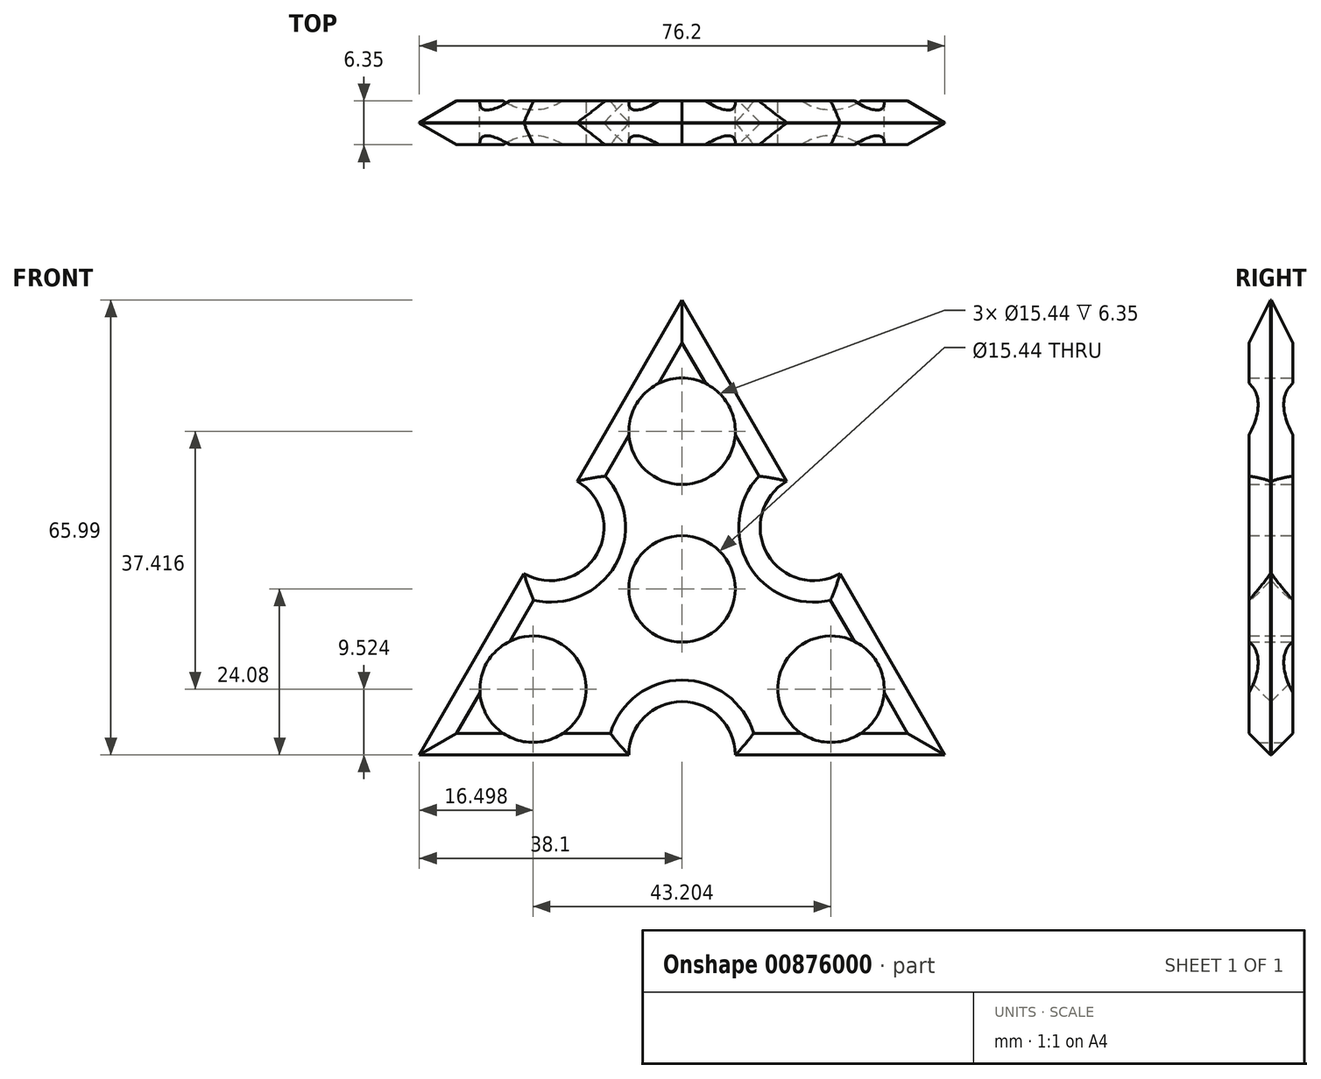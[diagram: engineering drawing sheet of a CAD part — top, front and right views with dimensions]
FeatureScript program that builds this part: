
annotation { "Feature Type Name" : "Feature", "Feature Type Description" : "" }
export const myFeature = defineFeature(function(context is Context, id is Id, definition is map)
    precondition{}
    {
        {
            var Q0;
            Q0=qCreatedBy(makeId("Front.planeOp"),FACE);
            var sketch = newSketch(context, id + "F0", { "sketchPlane" : qUnion([Q0])});
            skLineSegment(sketch, "E0", {"start": v(-38.1, -24.08) * mm, "end": v(0, 41.91) * mm});
            skLineSegment(sketch, "E1", {"start": v(0, 41.91) * mm, "end": v(38.1, -24.08) * mm});
            skLineSegment(sketch, "E2", {"start": v(38.1, -24.08) * mm, "end": v(-38.1, -24.08) * mm});
            skCircle(sketch, "E3", {"center": v(0, 22.86) * mm, "radius": 7.72 * mm});
            skCircle(sketch, "E4", {"center": v(21.6, -14.56) * mm, "radius": 7.72 * mm});
            skCircle(sketch, "E5", {"center": v(-21.6, -14.56) * mm, "radius": 7.72 * mm});
            skCircle(sketch, "E6", {"center": v(0, 0) * mm, "radius": 7.72 * mm});
            skCircle(sketch, "E7", {"center": v(-19.05, 8.91) * mm, "radius": 7.72 * mm});
            skCircle(sketch, "E8", {"center": v(19.05, 8.91) * mm, "radius": 7.72 * mm});
            skCircle(sketch, "E9", {"center": v(0, -24.08) * mm, "radius": 7.72 * mm});
            skSolve(sketch);
        }
        {
            var Q0;
            Q0=makeQuery(id+"F0.imprint","IMPRINT",FACE,{"disambiguationData":[TD([[makeQuery(id+"F0.imprint","IMPRINT",EDGE,{"derivedFrom":sQuery(id+"F0.wireOp",EDGE,"E3")}),-1.0]])]});
            extrude(context, id + "F1", {"entities" : qUnion([Q0]), "depth" : 6.35 * mm, "offsetDistance" : 25.4 * mm});
        }
        {
            var Q0;
            {var subQ0=sQuery(id+"F0.wireOp",EDGE,"E0");Q0=makeQuery(id+"F1.opExtrude","CAP_EDGE",EDGE,{"disambiguationData":[OSD([subQ0]),TDD([makeQuery(id+"F0.imprint","IMPRINT",EDGE,{"disambiguationData":[TD([[makeQuery(id+"F0.imprint","INTERSECT",VERTEX,{"derivedFrom":[subQ0,sQuery(id+"F0.wireOp",EDGE,"E2")]}),-1.0]])],"derivedFrom":subQ0})])],"isStart":false});}
            var Q1;
            Q1=makeQuery(id+"F1.opExtrude","CAP_EDGE",EDGE,{"disambiguationData":[OSD([sQuery(id+"F0.wireOp",EDGE,"E7")])],"isStart":false});
            var Q2;
            {var subQ0=sQuery(id+"F0.wireOp",EDGE,"E0");Q2=makeQuery(id+"F1.opExtrude","CAP_EDGE",EDGE,{"disambiguationData":[OSD([subQ0]),TDD([makeQuery(id+"F0.imprint","IMPRINT",EDGE,{"disambiguationData":[TD([[makeQuery(id+"F0.imprint","INTERSECT",VERTEX,{"derivedFrom":[subQ0,sQuery(id+"F0.wireOp",EDGE,"E1")]}),1.0]])],"derivedFrom":subQ0})])],"isStart":false});}
            var Q3;
            {var subQ0=sQuery(id+"F0.wireOp",EDGE,"E1");Q3=makeQuery(id+"F1.opExtrude","CAP_EDGE",EDGE,{"disambiguationData":[OSD([subQ0]),TDD([makeQuery(id+"F0.imprint","IMPRINT",EDGE,{"disambiguationData":[TD([[makeQuery(id+"F0.imprint","INTERSECT",VERTEX,{"derivedFrom":[sQuery(id+"F0.wireOp",EDGE,"E0"),subQ0]}),-1.0]])],"derivedFrom":subQ0})])],"isStart":false});}
            var Q4;
            Q4=makeQuery(id+"F1.opExtrude","CAP_EDGE",EDGE,{"disambiguationData":[OSD([sQuery(id+"F0.wireOp",EDGE,"E8")])],"isStart":false});
            var Q5;
            {var subQ0=sQuery(id+"F0.wireOp",EDGE,"E1");Q5=makeQuery(id+"F1.opExtrude","CAP_EDGE",EDGE,{"disambiguationData":[OSD([subQ0]),TDD([makeQuery(id+"F0.imprint","IMPRINT",EDGE,{"disambiguationData":[TD([[makeQuery(id+"F0.imprint","INTERSECT",VERTEX,{"derivedFrom":[subQ0,sQuery(id+"F0.wireOp",EDGE,"E2")]}),1.0]])],"derivedFrom":subQ0})])],"isStart":false});}
            var Q6;
            {var subQ0=sQuery(id+"F0.wireOp",EDGE,"E2");Q6=makeQuery(id+"F1.opExtrude","CAP_EDGE",EDGE,{"disambiguationData":[OSD([subQ0]),TDD([makeQuery(id+"F0.imprint","IMPRINT",EDGE,{"disambiguationData":[TD([[makeQuery(id+"F0.imprint","INTERSECT",VERTEX,{"derivedFrom":[sQuery(id+"F0.wireOp",EDGE,"E1"),subQ0]}),-1.0]])],"derivedFrom":subQ0})])],"isStart":false});}
            var Q7;
            Q7=makeQuery(id+"F1.opExtrude","CAP_EDGE",EDGE,{"disambiguationData":[OSD([sQuery(id+"F0.wireOp",EDGE,"E9")])],"isStart":false});
            var Q8;
            {var subQ0=sQuery(id+"F0.wireOp",EDGE,"E2");Q8=makeQuery(id+"F1.opExtrude","CAP_EDGE",EDGE,{"disambiguationData":[OSD([subQ0]),TDD([makeQuery(id+"F0.imprint","IMPRINT",EDGE,{"disambiguationData":[TD([[makeQuery(id+"F0.imprint","INTERSECT",VERTEX,{"derivedFrom":[sQuery(id+"F0.wireOp",EDGE,"E0"),subQ0]}),1.0]])],"derivedFrom":subQ0})])],"isStart":false});}
            var Q9;
            {var subQ0=sQuery(id+"F0.wireOp",EDGE,"E2");Q9=makeQuery(id+"F1.opExtrude","CAP_EDGE",EDGE,{"disambiguationData":[OSD([subQ0]),TDD([makeQuery(id+"F0.imprint","IMPRINT",EDGE,{"disambiguationData":[TD([[makeQuery(id+"F0.imprint","INTERSECT",VERTEX,{"derivedFrom":[sQuery(id+"F0.wireOp",EDGE,"E0"),subQ0]}),1.0]])],"derivedFrom":subQ0})])],"isStart":true});}
            var Q10;
            Q10=makeQuery(id+"F1.opExtrude","CAP_EDGE",EDGE,{"disambiguationData":[OSD([sQuery(id+"F0.wireOp",EDGE,"E9")])],"isStart":true});
            var Q11;
            {var subQ0=sQuery(id+"F0.wireOp",EDGE,"E2");Q11=makeQuery(id+"F1.opExtrude","CAP_EDGE",EDGE,{"disambiguationData":[OSD([subQ0]),TDD([makeQuery(id+"F0.imprint","IMPRINT",EDGE,{"disambiguationData":[TD([[makeQuery(id+"F0.imprint","INTERSECT",VERTEX,{"derivedFrom":[sQuery(id+"F0.wireOp",EDGE,"E1"),subQ0]}),-1.0]])],"derivedFrom":subQ0})])],"isStart":true});}
            var Q12;
            {var subQ0=sQuery(id+"F0.wireOp",EDGE,"E1");Q12=makeQuery(id+"F1.opExtrude","CAP_EDGE",EDGE,{"disambiguationData":[OSD([subQ0]),TDD([makeQuery(id+"F0.imprint","IMPRINT",EDGE,{"disambiguationData":[TD([[makeQuery(id+"F0.imprint","INTERSECT",VERTEX,{"derivedFrom":[subQ0,sQuery(id+"F0.wireOp",EDGE,"E2")]}),1.0]])],"derivedFrom":subQ0})])],"isStart":true});}
            var Q13;
            Q13=makeQuery(id+"F1.opExtrude","CAP_EDGE",EDGE,{"disambiguationData":[OSD([sQuery(id+"F0.wireOp",EDGE,"E8")])],"isStart":true});
            var Q14;
            {var subQ0=sQuery(id+"F0.wireOp",EDGE,"E1");Q14=makeQuery(id+"F1.opExtrude","CAP_EDGE",EDGE,{"disambiguationData":[OSD([subQ0]),TDD([makeQuery(id+"F0.imprint","IMPRINT",EDGE,{"disambiguationData":[TD([[makeQuery(id+"F0.imprint","INTERSECT",VERTEX,{"derivedFrom":[sQuery(id+"F0.wireOp",EDGE,"E0"),subQ0]}),-1.0]])],"derivedFrom":subQ0})])],"isStart":true});}
            var Q15;
            {var subQ0=sQuery(id+"F0.wireOp",EDGE,"E0");Q15=makeQuery(id+"F1.opExtrude","CAP_EDGE",EDGE,{"disambiguationData":[OSD([subQ0]),TDD([makeQuery(id+"F0.imprint","IMPRINT",EDGE,{"disambiguationData":[TD([[makeQuery(id+"F0.imprint","INTERSECT",VERTEX,{"derivedFrom":[subQ0,sQuery(id+"F0.wireOp",EDGE,"E1")]}),1.0]])],"derivedFrom":subQ0})])],"isStart":true});}
            var Q16;
            Q16=makeQuery(id+"F1.opExtrude","CAP_EDGE",EDGE,{"disambiguationData":[OSD([sQuery(id+"F0.wireOp",EDGE,"E7")])],"isStart":true});
            var Q17;
            {var subQ0=sQuery(id+"F0.wireOp",EDGE,"E0");Q17=makeQuery(id+"F1.opExtrude","CAP_EDGE",EDGE,{"disambiguationData":[OSD([subQ0]),TDD([makeQuery(id+"F0.imprint","IMPRINT",EDGE,{"disambiguationData":[TD([[makeQuery(id+"F0.imprint","INTERSECT",VERTEX,{"derivedFrom":[subQ0,sQuery(id+"F0.wireOp",EDGE,"E2")]}),-1.0]])],"derivedFrom":subQ0})])],"isStart":true});}
            chamfer(context, id + "F2", {"entities" : qUnion([Q0, Q1, Q2, Q3, Q4, Q5, Q6, Q7, Q8, Q9, Q10, Q11, Q12, Q13, Q14, Q15, Q16, Q17]), "width" : 3.12 * mm, "tangentPropagation" : true});
        }
    });
